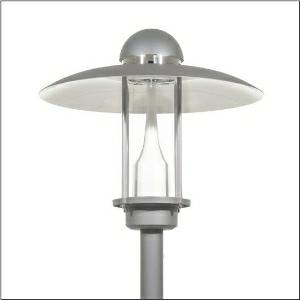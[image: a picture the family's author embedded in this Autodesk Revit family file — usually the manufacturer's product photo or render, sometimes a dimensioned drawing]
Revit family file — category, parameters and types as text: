
# Revit family: city-light_elegance_iq___p1_0a_5xa5265nf14h_5982
name_source: partatom
category: Lighting Fixtures
units: mm (PartAtom-declared; Revit-internal decimal feet)

## family parameters
Cut with Voids When Loaded = No
Host = Face
Light Source = No
Part Type = Normal
Room Calculation Point = No
Round Connector Dimension = Use Diameter
Shared = No

## types (1)
- --- (1 x LED, 1440 lm, 11.8 W, 2700K)
    Apparent Load = 12 VA
    CIE Flux Codes = 32 62 91 97 100
    Color Rendering = 70
    Color Temperature = 2700K
    Default Elevation = 1800 mm
    Description = City-Light Elegance iQ, mast luminaire, Module 540 iQ-SR, primary light control with 3 zone facetted reflector, of plastic, silver coated, highly specular, structured, primary optical cover: cover, of PMMA, transparent, light distribution: P1.0a, light emission: direct distribution, primary light characteristic: strongly asymmetric, installation type: post-top, LED, High Power LED, rated luminous flux: 1.440lm, luminous efficacy: 122lm/W, light colour: 727, colour temperature: 2700K, control gear: ECG iQ, control: presetting dimming logarithmic, Street-Remote, Auto-Match, Temp-Guard, Lumen-Switch, Night-Set, Smart-Wire, Light-Fading, Desk-Remote (wireless, voltage-free reading and setting of iQ features in the workshop via application-optimized NFC function/RFID function), optimised constant luminous flux control (CLO 2.0), with terminal, 6-pole, max. 2.5mm², mains connection: 220..240V, AC, 50/60Hz, start of lifetime: 12W, end of lifetime: 12W, reduction: 6W, luminaire housing, upper part, of aluminium, coated, Siteco® metallic grey (DB 702S), diameter: 750mm, height: 675mm, spigot size: d x l = 76 x 70mm (post-top) | with reducer (optional accessory) 60 x 70mm, post-top mast mounting element, of diecast aluminium, coated, Siteco® metallic grey (DB 702S), Module 540 iQ-SR, traffic white (RAL 9016), equipment: standard, protection rating (complete): IP65, insulation class (complete): insulation class II (safety insulation), certification: CE, ENEC, VDE, packaging unit: 1 piece

Light Distribution: P1.0a
    Height = 675 mm
    Lamp = 1 x LED
    Lamp Light Flux = 1440 lm
    Lamp Power = 11.8 W
    Lamp count = 1
    Length = 750 mm
    Luminous efficacy = 122 lm/W
    Manufacturer = Siteco
    ModVariant = No
    Model = 5XA5265NF14H
    Number of Poles = 1
    OnlyDefault = Yes
    Power Factor = 1
    Product Name = City-Light Elegance iQ | P1.0a
    Product group = mast luminaire | pylon top
    ProductGroupID = 6100
    Protection Class = Protection class II
    Protection Degree = IP 65
    RLX_Detail_Level = 1
    RlxData = <blob elided: 102037 chars, md5=5ccb5dcb>
    Socket = socket
    Standby Power = 0 W
    System Light Flux = 1440 lm
    System Power = 12 W
    Type Comments = factory setting: luminous flux: 100 % | dim-lin: 254 | 472 mA
    Type Image = l_1006912.jpg
    URL = http://relux.com
    VarID = @adj_063057
    Voltage = 0 V
    Weight = 0.00 kg
    Width = 0 mm  [stored 0 ft]

note: [stored X ft] marks values corroborated as IEEE doubles in the binary element streams (Revit-internal decimal feet)

## geometry (parser evidence)
native form markers: Blend x4, Sweep x11
no freeform markers — native parametric forms only
